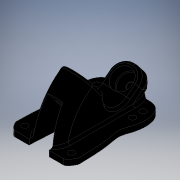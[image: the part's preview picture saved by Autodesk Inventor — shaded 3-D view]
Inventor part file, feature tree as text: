
AUTODESK INVENTOR PART (.ipt)
format: ipt  version: 2019 (Build 230136000, 136)  size: 1,243,648 bytes
history: native  units: mm
features: sketch x8, extrude x5, fillet x5, plane x4, other x3, revolve x1, loft x1, emboss x1
ambient origin geometry x8: Origin, YZ Plane, XZ Plane, XY Plane, X Axis, Y Axis, Z Axis, Center Point
bodies: Solid1 (feature_tree)
feature tree (28):
  extrude  "Extrusion8"  Depth=87.0mm
  plane  "Work Plane1"
  extrude  "Extrusion4"  Depth=49.0mm
  extrude  "Extrusion5"  Depth=55.0mm
  fillet  "Fillet3"  Radius=13.0mm
  fillet  "Fillet4"  Radius=21.0mm
  extrude  "Extrusion7"  Depth=5.0mm
  other  "Work Axis1"
  plane  "Work Plane2"
  revolve  "Revolution1"  [1 undecoded]
  fillet  "Fillet6"  Radius=80.0mm
  plane  "Work Plane5"
  sketch  "Sketch13"  dims[d275=12.5mm d284=25.0mm d285=0.0mm d286=80.0mm d287=0.0mm]
  plane  "Work Plane4"
  loft  "Loft1"
  extrude  "Extrusion9"  Depth=11.3mm
  fillet  "Fillet7"  Radius=12.5mm
  fillet  "Fillet8"  Radius=18.0mm
  emboss  "Emboss1"
  sketch  "Sketch2"  dims[d5=5.5mm d6=5.5mm d7=5.5mm d10=54.0mm d11=63.5mm d13=87.0mm]
  sketch  "Sketch4"  dims[d14=41.3mm d15=49.0mm]
  other  "Image6"
  sketch  "Sketch8"  dims[d16=57.0mm d17=55.0mm d217=13.0mm d218=21.0mm]
  sketch  "Sketch9"  dims[d219=5.0mm d221=8.0mm]
  sketch  "Sketch14"  dims[d345=80.0mm d346=80.0mm]
  other  "Image7"
  sketch  "Sketch16"  dims[d347=12.5mm d348=11.3mm d350=12.5mm d351=18.0mm]
  sketch  "Sketch17"  dims[d352=5.0mm d353=0.0mm d354=12.0mm d355=0.0mm d356=90.0deg d357=90.0deg d358=1.0mm d374=100.0mm d375=0.0mm d376=90.0deg d377=0.0mm d378=90.0deg d380=5.0mm d381=0.0mm d404=24.0mm d405=12.0mm d407=9.5mm d408=12.0mm d409=5.0mm d410=0.0mm d411=2.0mm d412=5.0mm d413=80.0mm d414=0.5mm d415=0.0mm]
note: 1 required parameter value undecoded (feature->parameter linkage not recoverable at this tier; creation-order binding heuristic only, values carry confidence <= 0.55)
